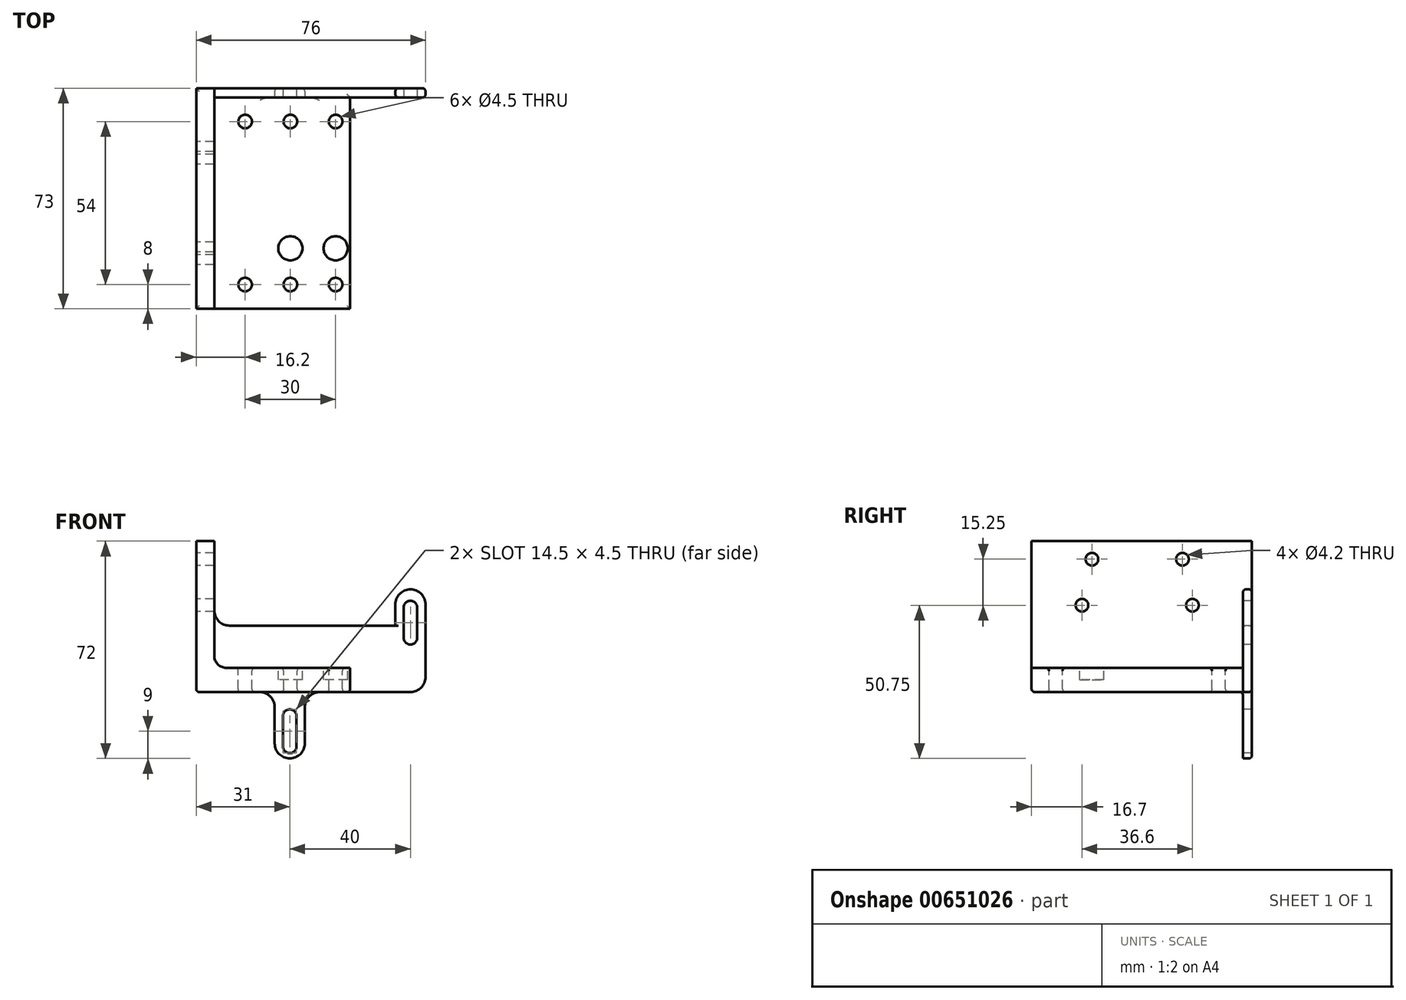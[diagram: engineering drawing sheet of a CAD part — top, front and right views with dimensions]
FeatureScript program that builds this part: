
annotation { "Feature Type Name" : "Feature", "Feature Type Description" : "" }
export const myFeature = defineFeature(function(context is Context, id is Id, definition is map)
    precondition{}
    {
        {
            var Q0;
            Q0=qCreatedBy(makeId("Top.planeOp"),FACE);
            var sketch = newSketch(context, id + "F0", { "sketchPlane" : qUnion([Q0])});
            skLineSegment(sketch, "E0.bottom", {"start": v(-45, 0) * mm, "end": v(0, 0) * mm});
            skLineSegment(sketch, "E0.top", {"start": v(-45, -70) * mm, "end": v(0, -70) * mm});
            skLineSegment(sketch, "E0.left", {"start": v(-45, 0) * mm, "end": v(-45, -70) * mm});
            skLineSegment(sketch, "E0.right", {"start": v(0, 0) * mm, "end": v(0, -70) * mm});
            skLineSegment(sketch, "E1.bottom", {"start": v(-34.8, -8) * mm, "end": v(-4.8, -8) * mm, "construction": true});
            skLineSegment(sketch, "E1.top", {"start": v(-34.8, -62) * mm, "end": v(-4.8, -62) * mm, "construction": true});
            skLineSegment(sketch, "E1.left", {"start": v(-34.8, -8) * mm, "end": v(-34.8, -62) * mm, "construction": true});
            skLineSegment(sketch, "E1.right", {"start": v(-4.8, -8) * mm, "end": v(-4.8, -62) * mm, "construction": true});
            skCircle(sketch, "E2", {"center": v(-4.8, -8) * mm, "radius": 2.25 * mm});
            skCircle(sketch, "E3", {"center": v(-34.8, -8) * mm, "radius": 2.25 * mm});
            skCircle(sketch, "E4", {"center": v(-34.8, -62) * mm, "radius": 2.25 * mm});
            skCircle(sketch, "E5", {"center": v(-4.8, -62) * mm, "radius": 2.25 * mm});
            skLineSegment(sketch, "E6", {"start": v(-19.8, -8) * mm, "end": v(-19.8, -62) * mm, "construction": true});
            skCircle(sketch, "E7", {"center": v(-19.8, -8) * mm, "radius": 2.25 * mm});
            skCircle(sketch, "E8", {"center": v(-19.8, -62) * mm, "radius": 2.25 * mm});
            skLineSegment(sketch, "E9", {"start": v(-34.8, -35) * mm, "end": v(-45, -35) * mm, "construction": true});
            skLineSegment(sketch, "E10.0", {"start": v(-34.8, -50) * mm, "end": v(-4.8, -50) * mm, "construction": true});
            skSolve(sketch);
        }
        {
            var Q0;
            Q0=qSketchRegion(id+"F0",true);
            extrude(context, id + "F1", {"entities" : qUnion([Q0]), "oppositeDirection" : true, "depth" : 8 * mm, "offsetDistance" : 25 * mm});
        }
        {
            var Q0;
            Q0=makeQuery(id+"F1.opExtrude","CAP_FACE",FACE,{"disambiguationData":[OSD([sQuery(id+"F0.wireOp",EDGE,"E0.bottom"),sQuery(id+"F0.wireOp",EDGE,"E0.top"),sQuery(id+"F0.wireOp",EDGE,"E0.left"),sQuery(id+"F0.wireOp",EDGE,"E0.right"),sQuery(id+"F0.wireOp",EDGE,"hVrX2CNV-9suW-4j3L-0wAi-LLcbi1nwGMZJ"),sQuery(id+"F0.wireOp",EDGE,"5PctEPi3-iVhW-VY0c-wPho-zEpeLB05UKu4"),sQuery(id+"F0.wireOp",EDGE,"6ss7uc4C-TfdB-fdjw-kezK-TaYYsvONMO77"),sQuery(id+"F0.wireOp",EDGE,"fzxmS708-5c4D-aOSR-16yi-becN9faOIMnc")])],"isStart":false});
            var sketch = newSketch(context, id + "F2", { "sketchPlane" : qUnion([Q0])});
            skLineSegment(sketch, "E11.bottom", {"start": v(-51, 70) * mm, "end": v(-45, 70) * mm});
            skLineSegment(sketch, "E11.top", {"start": v(-51, 0) * mm, "end": v(-45, 0) * mm});
            skLineSegment(sketch, "E11.left", {"start": v(-45, 70) * mm, "end": v(-45, 0) * mm});
            skLineSegment(sketch, "E11.right", {"start": v(-51, 70) * mm, "end": v(-51, 0) * mm});
            skSolve(sketch);
        }
        {
            var Q0;
            Q0=qSketchRegion(id+"F2",true);
            extrude(context, id + "F3", {"entities" : qUnion([Q0]), "operationType" : NewBodyOperationType.ADD, "oppositeDirection" : true, "depth" : 50 * mm, "offsetDistance" : 25 * mm});
        }
        {
            var Q0;
            Q0=makeQuery(id+"F3.opExtrude","SWEPT_FACE",FACE,{"disambiguationData":[OSD([sQuery(id+"F2.wireOp",EDGE,"E11.right")])]});
            var sketch = newSketch(context, id + "F4", { "sketchPlane" : qUnion([Q0])});
            skCircle(sketch, "E12", {"center": v(20, 36) * mm, "radius": 2.1 * mm});
            skCircle(sketch, "E13", {"center": v(50, 36) * mm, "radius": 2.1 * mm});
            skCircle(sketch, "E14", {"center": v(53.3, 20.75) * mm, "radius": 2.1 * mm});
            skCircle(sketch, "E15", {"center": v(16.7, 20.75) * mm, "radius": 2.1 * mm});
            skLineSegment(sketch, "E16", {"start": v(35, 42) * mm, "end": v(35, -8) * mm, "construction": true});
            skLineSegment(sketch, "E17", {"start": v(0, 17) * mm, "end": v(70, 17) * mm, "construction": true});
            skSolve(sketch);
        }
        {
            var Q0;
            Q0=qSketchRegion(id+"F4",true);
            var Q1;
            Q1=makeQuery(id+"F3.opExtrude","SWEPT_FACE",FACE,{"disambiguationData":[OSD([sQuery(id+"F2.wireOp",EDGE,"E11.left")])]});
            extrude(context, id + "F5", {"entities" : qUnion([Q0]), "operationType" : NewBodyOperationType.REMOVE, "endBound" : BoundingType.UP_TO_SURFACE, "oppositeDirection" : true, "depth" : 25 * mm, "endBoundEntityFace" : qUnion([Q1]), "offsetDistance" : 25 * mm});
        }
        {
            var Q0;
            Q0=makeQuery(id+"F1.opExtrude","CAP_FACE",FACE,{"disambiguationData":[OSD([sQuery(id+"F0.wireOp",EDGE,"E0.bottom"),sQuery(id+"F0.wireOp",EDGE,"E0.top"),sQuery(id+"F0.wireOp",EDGE,"E0.left"),sQuery(id+"F0.wireOp",EDGE,"E0.right"),sQuery(id+"F0.wireOp",EDGE,"E2"),sQuery(id+"F0.wireOp",EDGE,"E3"),sQuery(id+"F0.wireOp",EDGE,"E4"),sQuery(id+"F0.wireOp",EDGE,"E5"),sQuery(id+"F0.wireOp",EDGE,"E7"),sQuery(id+"F0.wireOp",EDGE,"E8"),sQuery(id+"F0.wireOp",EDGE,"D93dgR97-G6P7-6uv8-oJZd-jIXSzQyobwpD"),sQuery(id+"F0.wireOp",EDGE,"YrJNrxIA-OLu6-4XLX-susR-NArFQy6tvTXX")])],"isStart":true});
            var sketch = newSketch(context, id + "F6", { "sketchPlane" : qUnion([Q0])});
            skCircle(sketch, "E18", {"center": v(-19.8, -50) * mm, "radius": 4 * mm});
            skCircle(sketch, "E19", {"center": v(-4.8, -50) * mm, "radius": 4 * mm});
            skSolve(sketch);
        }
        {
            var Q0;
            Q0 = qSketchRegion(id + "F6", true);
            extrude(context, id + "F7", {"entities" : qUnion([Q0]), "operationType" : NewBodyOperationType.REMOVE, "oppositeDirection" : true, "depth" : 4 * mm, "offsetDistance" : 25 * mm});
        }
        {
            var Q0;
            Q0=makeQuery(id+"F3.boolean.opBoolean","MERGE",FACE,{"derivedFrom":[makeQuery(id+"F1.opExtrude","SWEPT_FACE",FACE,{"disambiguationData":[OSD([sQuery(id+"F0.wireOp",EDGE,"E0.bottom")])]}),makeQuery(id+"F3.opExtrude","SWEPT_FACE",FACE,{"disambiguationData":[OSD([sQuery(id+"F2.wireOp",EDGE,"E11.top")])]})]});
            var sketch = newSketch(context, id + "F8", { "sketchPlane" : qUnion([Q0])});
            skLineSegment(sketch, "E20.bottom", {"start": v(10, -8) * mm, "end": v(-20, -8) * mm});
            skLineSegment(sketch, "E20.top", {"start": v(40, 14) * mm, "end": v(-25, 14) * mm});
            skLineSegment(sketch, "E20.left", {"start": v(51, -8) * mm, "end": v(51, 14) * mm});
            skLineSegment(sketch, "E20.right", {"start": v(-25, -3) * mm, "end": v(-25, 14) * mm});
            skArc(sketch, "E21", {"start": v(-22.25, 10) * mm, "mid": v(-20, 7.75) * mm, "end": v(-17.75, 10) * mm});
            skLineSegment(sketch, "E22.bottom", {"start": v(-25, 14) * mm, "end": v(-15, 14) * mm});
            skLineSegment(sketch, "E22.top", {"start": v(-20, 26) * mm, "end": v(-20, 26) * mm});
            skLineSegment(sketch, "E22.left", {"start": v(-25, 14) * mm, "end": v(-25, 21) * mm});
            skLineSegment(sketch, "E22.right", {"start": v(-15, 14) * mm, "end": v(-15, 21) * mm});
            skArc(sketch, "E23", {"start": v(-17.75, 20) * mm, "mid": v(-20, 22.25) * mm, "end": v(-22.25, 20) * mm});
            skLineSegment(sketch, "E24", {"start": v(-17.75, 20) * mm, "end": v(-17.75, 10) * mm});
            skLineSegment(sketch, "E25", {"start": v(-22.25, 20) * mm, "end": v(-22.25, 10) * mm});
            skPoint(sketch, "E26.center.orphan", {"position": v(0, 7) * mm});
            skLineSegment(sketch, "E27.top", {"start": v(20, -30) * mm, "end": v(20, -30) * mm});
            skLineSegment(sketch, "E27.left", {"start": v(15, -13) * mm, "end": v(15, -25) * mm});
            skLineSegment(sketch, "E27.right", {"start": v(25, -13) * mm, "end": v(25, -25) * mm});
            skArc(sketch, "E28", {"start": v(17.75, -26) * mm, "mid": v(20, -28.25) * mm, "end": v(22.25, -26) * mm});
            skArc(sketch, "E29", {"start": v(22.25, -16) * mm, "mid": v(20, -13.75) * mm, "end": v(17.75, -16) * mm});
            skLineSegment(sketch, "E30", {"start": v(22.25, -16) * mm, "end": v(22.25, -26) * mm});
            skLineSegment(sketch, "E31", {"start": v(17.75, -16) * mm, "end": v(17.75, -26) * mm});
            skPoint(sketch, "E32.visualSharp", {"position": v(15, -30) * mm});
            skArc(sketch, "E32.filletArc", {"start": v(15, -25) * mm, "mid": v(16.46, -28.54) * mm, "end": v(20, -30) * mm});
            skPoint(sketch, "E33.visualSharp", {"position": v(25, -30) * mm});
            skArc(sketch, "E33.filletArc", {"start": v(20, -30) * mm, "mid": v(23.54, -28.54) * mm, "end": v(25, -25) * mm});
            skPoint(sketch, "E34.visualSharp", {"position": v(-25, -8) * mm});
            skArc(sketch, "E34.filletArc", {"start": v(-25, -3) * mm, "mid": v(-23.54, -6.54) * mm, "end": v(-20, -8) * mm});
            skPoint(sketch, "E35.visualSharp", {"position": v(-25, 26) * mm});
            skArc(sketch, "E35.filletArc", {"start": v(-20, 26) * mm, "mid": v(-23.54, 24.54) * mm, "end": v(-25, 21) * mm});
            skPoint(sketch, "E36.visualSharp", {"position": v(-15, 26) * mm});
            skArc(sketch, "E36.filletArc", {"start": v(-15, 21) * mm, "mid": v(-16.46, 24.54) * mm, "end": v(-20, 26) * mm});
            skArc(sketch, "E37.filletArc", {"start": v(15, -13) * mm, "mid": v(13.54, -9.46) * mm, "end": v(10, -8) * mm});
            skLineSegment(sketch, "E38", {"start": v(30, -8) * mm, "end": v(51, -8) * mm});
            skPoint(sketch, "E39.visualSharp", {"position": v(25, -8) * mm});
            skArc(sketch, "E39.filletArc", {"start": v(30, -8) * mm, "mid": v(26.46, -9.46) * mm, "end": v(25, -13) * mm});
            skLineSegment(sketch, "E40.bottom", {"start": v(45, 42) * mm, "end": v(51, 42) * mm});
            skLineSegment(sketch, "E40.top", {"start": v(45, 14) * mm, "end": v(51, 14) * mm});
            skLineSegment(sketch, "E40.left", {"start": v(45, 42) * mm, "end": v(45, 19) * mm});
            skLineSegment(sketch, "E40.right", {"start": v(51, 42) * mm, "end": v(51, 14) * mm});
            skArc(sketch, "E41.filletArc", {"start": v(40, 14) * mm, "mid": v(43.54, 15.46) * mm, "end": v(45, 19) * mm});
            skSolve(sketch);
        }
        {
            var Q0;
            Q0 = qSketchRegion(id + "F8", true);
            extrude(context, id + "F9", {"entities" : qUnion([Q0]), "operationType" : NewBodyOperationType.ADD, "depth" : 3 * mm, "offsetDistance" : 25 * mm});
        }
        {
            var Q0;
            Q0=makeQuery(id+"F3.boolean.opBoolean","MERGE",FACE,{"derivedFrom":[makeQuery(id+"F1.opExtrude","SWEPT_FACE",FACE,{"disambiguationData":[OSD([sQuery(id+"F0.wireOp",EDGE,"E0.top")])]}),makeQuery(id+"F3.opExtrude","SWEPT_FACE",FACE,{"disambiguationData":[OSD([sQuery(id+"F2.wireOp",EDGE,"E11.bottom")])]})]});
            var sketch = newSketch(context, id + "F10", { "sketchPlane" : qUnion([Q0])});
            skLineSegment(sketch, "E42.0", {"start": v(-45, 42) * mm, "end": v(-45, 4) * mm});
            skLineSegment(sketch, "E43.0", {"start": v(-41, 0) * mm, "end": v(0, 0) * mm});
            skPoint(sketch, "E44.visualSharp", {"position": v(-45, 0) * mm});
            skArc(sketch, "E44.filletArc", {"start": v(-45, 4) * mm, "mid": v(-43.83, 1.17) * mm, "end": v(-41, 0) * mm});
            skLineSegment(sketch, "E45", {"start": v(-41, 0) * mm, "end": v(-45, 0) * mm});
            skLineSegment(sketch, "E46", {"start": v(-45, 0) * mm, "end": v(-45, 4) * mm});
            skSolve(sketch);
        }
        {
            var Q0;
            Q0 = qSketchRegion(id + "F10", true);
            extrude(context, id + "F11", {"entities" : qUnion([Q0]), "operationType" : NewBodyOperationType.ADD, "endBound" : BoundingType.UP_TO_NEXT, "oppositeDirection" : true, "depth" : 25 * mm, "offsetDistance" : 25 * mm});
        }
        {
            var Q0;
            Q0=makeQuery(id+"F1.opExtrude","CAP_EDGE",EDGE,{"disambiguationData":[OSD([sQuery(id+"F0.wireOp",EDGE,"E5")])],"isStart":true});
            var Q1;
            Q1=makeQuery(id+"F1.opExtrude","CAP_EDGE",EDGE,{"disambiguationData":[OSD([sQuery(id+"F0.wireOp",EDGE,"E8")])],"isStart":true});
            var Q2;
            Q2=makeQuery(id+"F1.opExtrude","CAP_EDGE",EDGE,{"disambiguationData":[OSD([sQuery(id+"F0.wireOp",EDGE,"E4")])],"isStart":true});
            var Q3;
            Q3=makeQuery(id+"F7.boolean.opBoolean","COPY",EDGE,{"derivedFrom":makeQuery(id+"F7.opExtrude","CAP_EDGE",EDGE,{"disambiguationData":[OSD([sQuery(id+"F6.wireOp",EDGE,"E18")])],"isStart":true})});
            var Q4;
            Q4=makeQuery(id+"F7.boolean.opBoolean","COPY",EDGE,{"derivedFrom":makeQuery(id+"F7.opExtrude","CAP_EDGE",EDGE,{"disambiguationData":[OSD([sQuery(id+"F6.wireOp",EDGE,"E19")])],"isStart":true})});
            var Q5;
            Q5=makeQuery(id+"F1.opExtrude","CAP_EDGE",EDGE,{"disambiguationData":[OSD([sQuery(id+"F0.wireOp",EDGE,"E2")])],"isStart":true});
            var Q6;
            Q6=makeQuery(id+"F1.opExtrude","CAP_EDGE",EDGE,{"disambiguationData":[OSD([sQuery(id+"F0.wireOp",EDGE,"E7")])],"isStart":true});
            var Q7;
            Q7=makeQuery(id+"F1.opExtrude","CAP_EDGE",EDGE,{"disambiguationData":[OSD([sQuery(id+"F0.wireOp",EDGE,"E3")])],"isStart":true});
            var Q8;
            Q8=makeQuery(id+"F5.boolean.opBoolean","COPY",EDGE,{"derivedFrom":makeQuery(id+"F5.opExtrude","TWEAK_EDGE",EDGE,{"derivedFrom":[makeQuery(id+"F3.opExtrude","SWEPT_FACE",FACE,{"disambiguationData":[OSD([sQuery(id+"F2.wireOp",EDGE,"E11.left")])]}),makeQuery(id+"F4.imprint","IMPRINT",EDGE,{"derivedFrom":sQuery(id+"F4.wireOp",EDGE,"E14")})]})});
            var Q9;
            Q9=makeQuery(id+"F5.boolean.opBoolean","COPY",EDGE,{"derivedFrom":makeQuery(id+"F5.opExtrude","TWEAK_EDGE",EDGE,{"derivedFrom":[makeQuery(id+"F3.opExtrude","SWEPT_FACE",FACE,{"disambiguationData":[OSD([sQuery(id+"F2.wireOp",EDGE,"E11.left")])]}),makeQuery(id+"F4.imprint","IMPRINT",EDGE,{"derivedFrom":sQuery(id+"F4.wireOp",EDGE,"E13")})]})});
            var Q10;
            Q10=makeQuery(id+"F5.boolean.opBoolean","COPY",EDGE,{"derivedFrom":makeQuery(id+"F5.opExtrude","TWEAK_EDGE",EDGE,{"derivedFrom":[makeQuery(id+"F3.opExtrude","SWEPT_FACE",FACE,{"disambiguationData":[OSD([sQuery(id+"F2.wireOp",EDGE,"E11.left")])]}),makeQuery(id+"F4.imprint","IMPRINT",EDGE,{"derivedFrom":sQuery(id+"F4.wireOp",EDGE,"E12")})]})});
            var Q11;
            Q11=makeQuery(id+"F5.boolean.opBoolean","COPY",EDGE,{"derivedFrom":makeQuery(id+"F5.opExtrude","TWEAK_EDGE",EDGE,{"derivedFrom":[makeQuery(id+"F3.opExtrude","SWEPT_FACE",FACE,{"disambiguationData":[OSD([sQuery(id+"F2.wireOp",EDGE,"E11.left")])]}),makeQuery(id+"F4.imprint","IMPRINT",EDGE,{"derivedFrom":sQuery(id+"F4.wireOp",EDGE,"E15")})]})});
            var Q12;
            Q12=makeQuery(id+"F5.boolean.opBoolean","COPY",EDGE,{"derivedFrom":makeQuery(id+"F5.opExtrude","CAP_EDGE",EDGE,{"disambiguationData":[OSD([sQuery(id+"F4.wireOp",EDGE,"E12")])],"isStart":true})});
            var Q13;
            Q13=makeQuery(id+"F5.boolean.opBoolean","COPY",EDGE,{"derivedFrom":makeQuery(id+"F5.opExtrude","CAP_EDGE",EDGE,{"disambiguationData":[OSD([sQuery(id+"F4.wireOp",EDGE,"E15")])],"isStart":true})});
            var Q14;
            Q14=makeQuery(id+"F5.boolean.opBoolean","COPY",EDGE,{"derivedFrom":makeQuery(id+"F5.opExtrude","CAP_EDGE",EDGE,{"disambiguationData":[OSD([sQuery(id+"F4.wireOp",EDGE,"E14")])],"isStart":true})});
            var Q15;
            Q15=makeQuery(id+"F5.boolean.opBoolean","COPY",EDGE,{"derivedFrom":makeQuery(id+"F5.opExtrude","CAP_EDGE",EDGE,{"disambiguationData":[OSD([sQuery(id+"F4.wireOp",EDGE,"E13")])],"isStart":true})});
            var Q16;
            Q16=makeQuery(id+"F1.opExtrude","CAP_EDGE",EDGE,{"disambiguationData":[OSD([sQuery(id+"F0.wireOp",EDGE,"E2")])],"isStart":false});
            var Q17;
            Q17=makeQuery(id+"F1.opExtrude","CAP_EDGE",EDGE,{"disambiguationData":[OSD([sQuery(id+"F0.wireOp",EDGE,"E7")])],"isStart":false});
            var Q18;
            Q18=makeQuery(id+"F1.opExtrude","CAP_EDGE",EDGE,{"disambiguationData":[OSD([sQuery(id+"F0.wireOp",EDGE,"D93dgR97-G6P7-6uv8-oJZd-jIXSzQyobwpD")])],"isStart":false});
            var Q19;
            Q19=makeQuery(id+"F1.opExtrude","CAP_EDGE",EDGE,{"disambiguationData":[OSD([sQuery(id+"F0.wireOp",EDGE,"E5")])],"isStart":false});
            var Q20;
            Q20=makeQuery(id+"F1.opExtrude","CAP_EDGE",EDGE,{"disambiguationData":[OSD([sQuery(id+"F0.wireOp",EDGE,"E4")])],"isStart":false});
            var Q21;
            Q21=makeQuery(id+"F1.opExtrude","CAP_EDGE",EDGE,{"disambiguationData":[OSD([sQuery(id+"F0.wireOp",EDGE,"E8")])],"isStart":false});
            var Q22;
            Q22=makeQuery(id+"F9.boolean.opBoolean","MERGE",FACE,{"derivedFrom":[makeQuery(id+"F3.boolean.opBoolean","MERGE",FACE,{"derivedFrom":[makeQuery(id+"F1.opExtrude","CAP_FACE",FACE,{"disambiguationData":[OSD([sQuery(id+"F0.wireOp",EDGE,"E0.bottom"),sQuery(id+"F0.wireOp",EDGE,"E0.top"),sQuery(id+"F0.wireOp",EDGE,"E0.left"),sQuery(id+"F0.wireOp",EDGE,"E0.right"),sQuery(id+"F0.wireOp",EDGE,"E2"),sQuery(id+"F0.wireOp",EDGE,"E3"),sQuery(id+"F0.wireOp",EDGE,"E4"),sQuery(id+"F0.wireOp",EDGE,"E5"),sQuery(id+"F0.wireOp",EDGE,"E7"),sQuery(id+"F0.wireOp",EDGE,"E8"),sQuery(id+"F0.wireOp",EDGE,"D93dgR97-G6P7-6uv8-oJZd-jIXSzQyobwpD"),sQuery(id+"F0.wireOp",EDGE,"YrJNrxIA-OLu6-4XLX-susR-NArFQy6tvTXX")])],"isStart":false}),makeQuery(id+"F3.opExtrude","CAP_FACE",FACE,{"disambiguationData":[OSD([sQuery(id+"F2.wireOp",EDGE,"E11.bottom"),sQuery(id+"F2.wireOp",EDGE,"E11.top"),sQuery(id+"F2.wireOp",EDGE,"E11.left"),sQuery(id+"F2.wireOp",EDGE,"E11.right")])],"isStart":true})]}),makeQuery(id+"F9.opExtrude","SWEPT_FACE",FACE,{"disambiguationData":[OSD([sQuery(id+"F8.wireOp",EDGE,"E20.bottom")])]}),makeQuery(id+"F9.opExtrude","SWEPT_FACE",FACE,{"disambiguationData":[OSD([sQuery(id+"F8.wireOp",EDGE,"E38")])]})]});
            fillet(context, id + "F12", {"entities" : qUnion([Q0, Q1, Q2, Q3, Q4, Q5, Q6, Q7, Q8, Q9, Q10, Q11, Q12, Q13, Q14, Q15, Q16, Q17, Q18, Q19, Q20, Q21, Q22]), "radius" : 1 * mm, "tangentPropagation" : true, "allowEdgeOverflow" : false});
        }
    });
